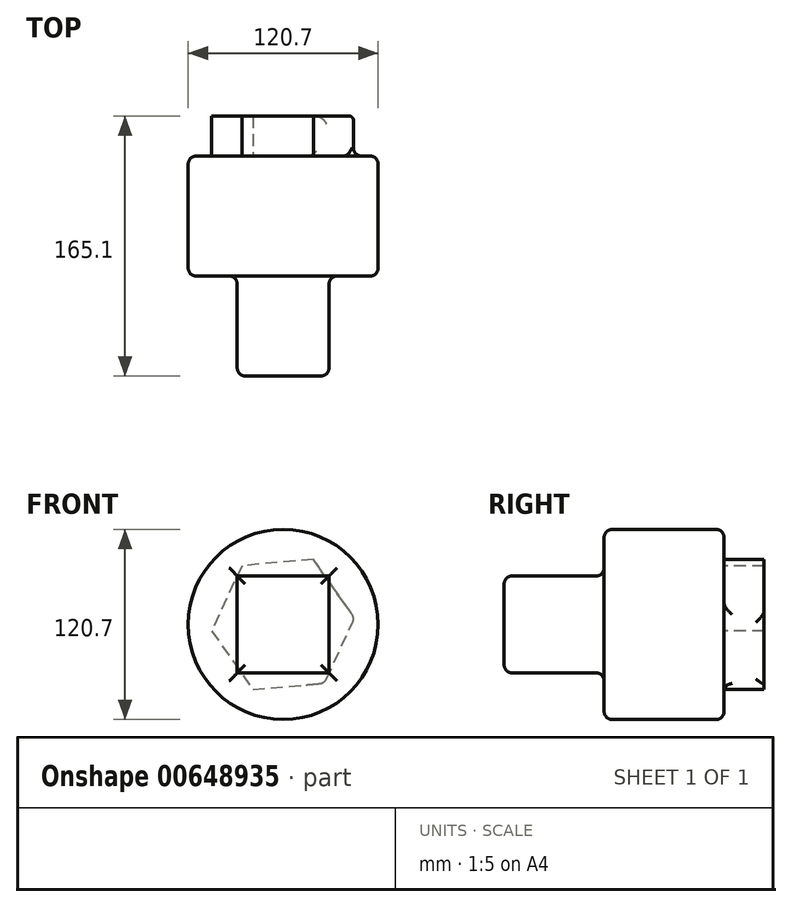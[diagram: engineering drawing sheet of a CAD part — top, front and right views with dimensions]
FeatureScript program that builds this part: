
annotation { "Feature Type Name" : "Feature", "Feature Type Description" : "" }
export const myFeature = defineFeature(function(context is Context, id is Id, definition is map)
    precondition{}
    {
        {
            var Q0;
            Q0=qCreatedBy(makeId("Front.planeOp"),FACE);
            var sketch = newSketch(context, id + "F0", { "sketchPlane" : qUnion([Q0])});
            skCircle(sketch, "E0", {"center": v(0, 0) * mm, "radius": 60.35 * mm});
            skSolve(sketch);
        }
        {
            var Q0;
            Q0=makeQuery(id+"F0.imprint","IMPRINT",FACE,{"disambiguationData":[TD([[makeQuery(id+"F0.imprint","IMPRINT",EDGE,{"derivedFrom":sQuery(id+"F0.wireOp",EDGE,"E0")}),1.0]])]});
            extrude(context, id + "F1", {"entities" : qUnion([Q0]), "depth" : 76.2 * mm, "offsetDistance" : 25.4 * mm});
        }
        {
            var Q0;
            Q0=makeQuery(id+"F1.opExtrude","CAP_FACE",FACE,{"disambiguationData":[OSD([sQuery(id+"F0.wireOp",EDGE,"E0")])],"isStart":false});
            var sketch = newSketch(context, id + "F2", { "sketchPlane" : qUnion([Q0])});
            skSolve(sketch);
        }
        {
            var Q0;
            Q0=makeQuery(id+"F2.imprint","IMPRINT",FACE,{"disambiguationData":[TD([[makeQuery(id+"F2.imprint","IMPRINT",EDGE,{"derivedFrom":makeQuery(id+"F1.opExtrude","CAP_EDGE",EDGE,{"disambiguationData":[OSD([sQuery(id+"F0.wireOp",EDGE,"E0")])],"isStart":false})}),1.0]])]});
            var sketch = newSketch(context, id + "F3", { "sketchPlane" : qUnion([Q0])});
            skLineSegment(sketch, "E1.bottom", {"start": v(29.15, -30.79) * mm, "end": v(-29.15, -30.79) * mm});
            skLineSegment(sketch, "E1.top", {"start": v(29.15, 30.79) * mm, "end": v(-29.15, 30.79) * mm});
            skLineSegment(sketch, "E1.left", {"start": v(29.15, -30.79) * mm, "end": v(29.15, 30.79) * mm});
            skLineSegment(sketch, "E1.right", {"start": v(-29.15, -30.79) * mm, "end": v(-29.15, 30.79) * mm});
            skPoint(sketch, "E1.middle", {"position": v(0, 0) * mm});
            skSolve(sketch);
        }
        {
            var Q0;
            Q0=makeQuery(id+"F3.imprint","IMPRINT",FACE,{"disambiguationData":[TD([[makeQuery(id+"F3.imprint","IMPRINT",EDGE,{"derivedFrom":sQuery(id+"F3.wireOp",EDGE,"E1.bottom")}),-1.0]])]});
            extrude(context, id + "F4", {"entities" : qUnion([Q0]), "operationType" : NewBodyOperationType.ADD, "depth" : 63.5 * mm, "offsetDistance" : 25.4 * mm});
        }
        {
            var Q0;
            Q0=makeQuery(id+"F1.opExtrude","CAP_FACE",FACE,{"disambiguationData":[OSD([sQuery(id+"F0.wireOp",EDGE,"E0")])],"isStart":true});
            var sketch = newSketch(context, id + "F5", { "sketchPlane" : qUnion([Q0])});
            skCircle(sketch, "E2.cCircle", {"center": v(0, 0) * mm, "radius": 39.48 * mm, "construction": true});
            skLineSegment(sketch, "E2.0", {"start": v(26.25, 37.28) * mm, "end": v(45.4, -4.09) * mm});
            skLineSegment(sketch, "E2.1", {"start": v(45.4, -4.09) * mm, "end": v(19.16, -41.37) * mm});
            skLineSegment(sketch, "E2.2", {"start": v(19.16, -41.37) * mm, "end": v(-26.25, -37.28) * mm});
            skLineSegment(sketch, "E2.3", {"start": v(-26.25, -37.28) * mm, "end": v(-45.4, 4.09) * mm});
            skLineSegment(sketch, "E2.4", {"start": v(-45.4, 4.09) * mm, "end": v(-19.16, 41.37) * mm});
            skLineSegment(sketch, "E2.5", {"start": v(-19.16, 41.37) * mm, "end": v(26.25, 37.28) * mm});
            skPoint(sketch, "E2.0.midPoint", {"position": v(35.83, 16.6) * mm});
            skSolve(sketch);
        }
        {
            var Q0;
            Q0 = qSketchRegion(id + "F5", true);
            var sketch = newSketch(context, id + "F6", { "sketchPlane" : qUnion([Q0])});
            skSolve(sketch);
        }
        {
            var Q0;
            Q0=makeQuery(id+"F6.imprint","IMPRINT",FACE,{"disambiguationData":[TD([[makeQuery(id+"F6.imprint","IMPRINT",EDGE,{"derivedFrom":makeQuery(id+"F5.imprint","IMPRINT",EDGE,{"derivedFrom":sQuery(id+"F5.wireOp",EDGE,"E2.0")})}),-1.0]])]});
            extrude(context, id + "F7", {"entities" : qUnion([Q0]), "operationType" : NewBodyOperationType.ADD, "depth" : 25.4 * mm, "offsetDistance" : 25.4 * mm});
        }
        {
            var Q0;
            Q0=makeQuery(id+"F7.opExtrude","SWEPT_FACE",FACE,{"disambiguationData":[OSD([sQuery(id+"F5.wireOp",EDGE,"E2.3")])]});
            fillet(context, id + "F8", {"entities" : qUnion([Q0]), "radius" : 5.08 * mm, "tangentPropagation" : true, "allowEdgeOverflow" : false});
        }
        {
            var Q0;
            Q0=makeQuery(id+"F4.opExtrude","CAP_FACE",FACE,{"disambiguationData":[OSD([sQuery(id+"F3.wireOp",EDGE,"E1.bottom"),sQuery(id+"F3.wireOp",EDGE,"E1.top"),sQuery(id+"F3.wireOp",EDGE,"E1.left"),sQuery(id+"F3.wireOp",EDGE,"E1.right")])],"isStart":false});
            var Q1;
            Q1=makeQuery(id+"F1.opExtrude","CAP_FACE",FACE,{"disambiguationData":[OSD([sQuery(id+"F0.wireOp",EDGE,"E0")])],"isStart":false});
            fillet(context, id + "F9", {"entities" : qUnion([Q0, Q1]), "radius" : 5.08 * mm, "tangentPropagation" : true, "allowEdgeOverflow" : false});
        }
        {
            var Q0;
            Q0=makeQuery(id+"F1.opExtrude","CAP_EDGE",EDGE,{"disambiguationData":[OSD([sQuery(id+"F0.wireOp",EDGE,"E0")])],"isStart":true});
            fillet(context, id + "F10", {"entities" : qUnion([Q0]), "radius" : 5.08 * mm, "tangentPropagation" : true, "allowEdgeOverflow" : false});
        }
    });
